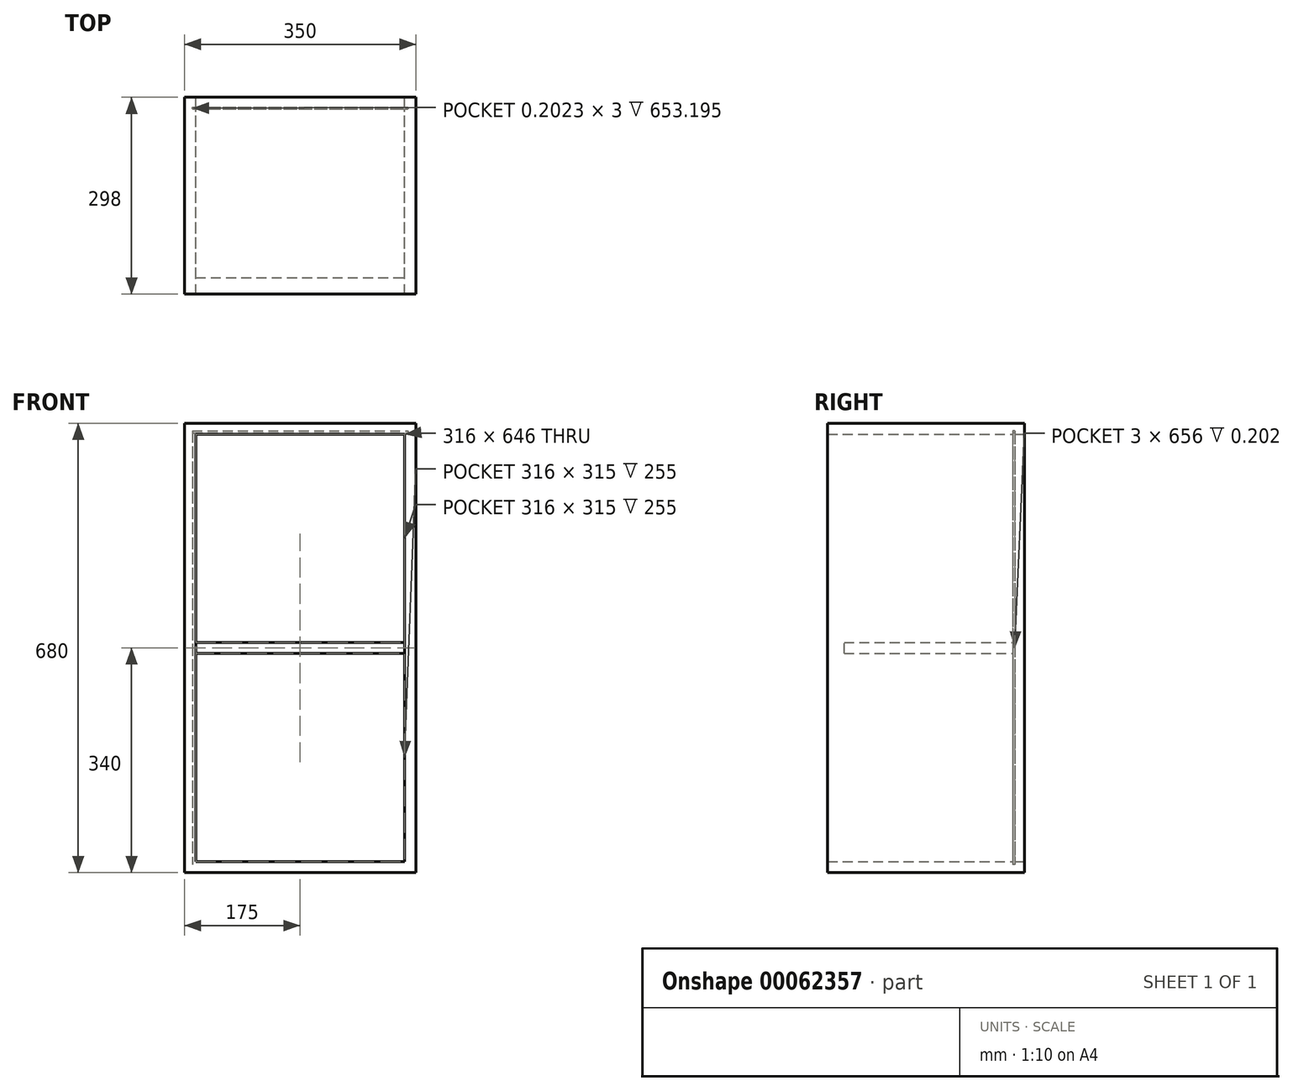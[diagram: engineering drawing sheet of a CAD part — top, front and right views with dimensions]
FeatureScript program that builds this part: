
annotation { "Feature Type Name" : "Feature", "Feature Type Description" : "" }
export const myFeature = defineFeature(function(context is Context, id is Id, definition is map)
    precondition{}
    {
        {
            var Q0;
            Q0=qCreatedBy(makeId("Front.planeOp"),FACE);
            var sketch = newSketch(context, id + "F0", { "sketchPlane" : qUnion([Q0])});
            skLineSegment(sketch, "E0", {"start": v(-175, 340) * mm, "end": v(-175, -340) * mm});
            skLineSegment(sketch, "E1", {"start": v(-175, 340) * mm, "end": v(-158, 323) * mm});
            skLineSegment(sketch, "E2", {"start": v(-158, 323) * mm, "end": v(-158, -323) * mm});
            skLineSegment(sketch, "E3", {"start": v(-158, -323) * mm, "end": v(-175, -340) * mm});
            skLineSegment(sketch, "E4", {"start": v(-175, 340) * mm, "end": v(0, 340) * mm});
            skLineSegment(sketch, "E5", {"start": v(-158, 323) * mm, "end": v(0, 323) * mm});
            skLineSegment(sketch, "E6", {"start": v(-158, -323) * mm, "end": v(0, -323) * mm});
            skLineSegment(sketch, "E7", {"start": v(-175, -340) * mm, "end": v(0, -340) * mm});
            skLineSegment(sketch, "E8", {"start": v(0, 391.01) * mm, "end": v(0, -441.6) * mm, "construction": true});
            skLineSegment(sketch, "E9.MirrorCS", {"start": v(175, 340) * mm, "end": v(0, 340) * mm});
            skLineSegment(sketch, "E10.MirrorCS", {"start": v(158, 323) * mm, "end": v(0, 323) * mm});
            skLineSegment(sketch, "E11.MirrorCS", {"start": v(175, 340) * mm, "end": v(158, 323) * mm});
            skLineSegment(sketch, "E12.MirrorCS", {"start": v(158, 323) * mm, "end": v(158, -323) * mm});
            skLineSegment(sketch, "E13.MirrorCS", {"start": v(175, 340) * mm, "end": v(175, -340) * mm});
            skLineSegment(sketch, "E14.MirrorCS", {"start": v(158, -323) * mm, "end": v(0, -323) * mm});
            skLineSegment(sketch, "E15.MirrorCS", {"start": v(175, -340) * mm, "end": v(0, -340) * mm});
            skLineSegment(sketch, "E16.MirrorCS", {"start": v(158, -323) * mm, "end": v(175, -340) * mm});
            skLineSegment(sketch, "E17", {"start": v(-158, -8) * mm, "end": v(158, -8) * mm});
            skLineSegment(sketch, "E18", {"start": v(158, -8) * mm, "end": v(158, 8) * mm});
            skLineSegment(sketch, "E19", {"start": v(158, 8) * mm, "end": v(-158, 8) * mm});
            skLineSegment(sketch, "E20", {"start": v(-158, 8) * mm, "end": v(-158, -8) * mm});
            skLineSegment(sketch, "E21", {"start": v(-295.4, 0) * mm, "end": v(343.1, 0) * mm, "construction": true});
            skSolve(sketch);
        }
        {
            var Q0;
            Q0=makeQuery(id+"F0.imprint","IMPRINT",FACE,{"disambiguationData":[TD([[makeQuery(id+"F0.imprint","IMPRINT",EDGE,{"derivedFrom":sQuery(id+"F0.wireOp",EDGE,"E1")}),1.0]])]});
            var Q1;
            Q1=makeQuery(id+"F0.imprint","IMPRINT",FACE,{"disambiguationData":[TD([[makeQuery(id+"F0.imprint","IMPRINT",EDGE,{"derivedFrom":sQuery(id+"F0.wireOp",EDGE,"E3")}),1.0]])]});
            var Q2;
            Q2=makeQuery(id+"F0.imprint","IMPRINT",FACE,{"disambiguationData":[TD([[makeQuery(id+"F0.imprint","IMPRINT",EDGE,{"derivedFrom":sQuery(id+"F0.wireOp",EDGE,"E0")}),1.0]])]});
            var Q3;
            {var subQ3=sQuery(id+"F0.wireOp",EDGE,"E11.MirrorCS");Q3=makeQuery(id+"F0.imprint","IMPRINT",FACE,{"disambiguationData":[TD([[makeQuery(id+"F0.imprint","IMPRINT",EDGE,{"derivedFrom":subQ3}),1.0]])]});}
            var Q4;
            Q4=makeQuery(id+"F0.imprint","IMPRINT",FACE,{"disambiguationData":[TD([[makeQuery(id+"F0.imprint","IMPRINT",EDGE,{"derivedFrom":sQuery(id+"F0.wireOp",EDGE,"E17")}),1.0]])]});
            var Q5;
            Q5=sQuery(id+"F0.wireOp",EDGE,"E0");
            var Q6;
            Q6=sQuery(id+"F0.wireOp",EDGE,"E2");
            extrude(context, id + "F1", {"entities" : qUnion([Q0, Q1, Q2, Q3, Q4]), "surfaceEntities" : qUnion([Q5, Q6]), "depth" : 280 * mm, "hasSecondDirection" : true, "secondDirectionOppositeDirection" : true, "secondDirectionDepth" : 18 * mm});
        }
        {
            var Q0;
            Q0=makeQuery(id+"F1.opExtrude","SWEPT_FACE",FACE,{"disambiguationData":[OSD([sQuery(id+"F0.wireOp",EDGE,"E19")])]});
            var sketch = newSketch(context, id + "F2", { "sketchPlane" : qUnion([Q0])});
            skLineSegment(sketch, "E22.bottom", {"start": v(-158, -280) * mm, "end": v(158, -280) * mm});
            skLineSegment(sketch, "E22.top", {"start": v(-158, -255) * mm, "end": v(158, -255) * mm});
            skLineSegment(sketch, "E22.left", {"start": v(-158, -280) * mm, "end": v(-158, -255) * mm});
            skLineSegment(sketch, "E22.right", {"start": v(158, -280) * mm, "end": v(158, -255) * mm});
            skSolve(sketch);
        }
        {
            var Q0;
            Q0=makeQuery(id+"F2.imprint","IMPRINT",FACE,{"disambiguationData":[TD([[makeQuery(id+"F2.imprint","IMPRINT",EDGE,{"derivedFrom":sQuery(id+"F2.wireOp",EDGE,"E22.bottom")}),-1.0]])]});
            extrude(context, id + "F3", {"entities" : qUnion([Q0]), "operationType" : NewBodyOperationType.REMOVE, "oppositeDirection" : true, "depth" : 16 * mm});
        }
        {
            var Q0;
            Q0=makeQuery(id+"F1.opExtrude","SWEPT_FACE",FACE,{"disambiguationData":[OSD([sQuery(id+"F0.wireOp",EDGE,"E17")])]});
            var sketch = newSketch(context, id + "F4", { "sketchPlane" : qUnion([Q0])});
            skLineSegment(sketch, "E23.bottom", {"start": v(-158, -18) * mm, "end": v(158, -18) * mm});
            skLineSegment(sketch, "E23.top", {"start": v(-158, 0) * mm, "end": v(158, 0) * mm});
            skLineSegment(sketch, "E23.left", {"start": v(-158, -18) * mm, "end": v(-158, 0) * mm});
            skLineSegment(sketch, "E23.right", {"start": v(158, -18) * mm, "end": v(158, 0) * mm});
            skSolve(sketch);
        }
        {
            var Q0;
            Q0=makeQuery(id+"F4.imprint","IMPRINT",FACE,{"disambiguationData":[TD([[makeQuery(id+"F4.imprint","IMPRINT",EDGE,{"derivedFrom":sQuery(id+"F4.wireOp",EDGE,"E23.bottom")}),1.0]])]});
            extrude(context, id + "F5", {"entities" : qUnion([Q0]), "operationType" : NewBodyOperationType.REMOVE, "oppositeDirection" : true, "depth" : 16 * mm});
        }
        {
            var Q0;
            Q0=qCreatedBy(makeId("Front.planeOp"),FACE);
            var sketch = newSketch(context, id + "F6", { "sketchPlane" : qUnion([Q0])});
            skLineSegment(sketch, "E24.bottom", {"start": v(-163, 328) * mm, "end": v(163, 328) * mm});
            skLineSegment(sketch, "E24.top", {"start": v(-163, -328) * mm, "end": v(163, -328) * mm});
            skLineSegment(sketch, "E24.left", {"start": v(-163, 328) * mm, "end": v(-163, -328) * mm});
            skLineSegment(sketch, "E24.right", {"start": v(163, 328) * mm, "end": v(163, -328) * mm});
            skLineSegment(sketch, "E25", {"start": v(0, 407.56) * mm, "end": v(0, -373.9) * mm, "construction": true});
            skLineSegment(sketch, "E26", {"start": v(-220.81, 0) * mm, "end": v(218.39, 0) * mm, "construction": true});
            skSolve(sketch);
        }
        {
            var Q0;
            Q0=makeQuery(id+"F6.imprint","IMPRINT",FACE,{"disambiguationData":[TD([[makeQuery(id+"F6.imprint","IMPRINT",EDGE,{"derivedFrom":sQuery(id+"F6.wireOp",EDGE,"E24.bottom")}),-1.0]])]});
            extrude(context, id + "F7", {"entities" : qUnion([Q0]), "operationType" : NewBodyOperationType.REMOVE, "oppositeDirection" : true, "depth" : 3 * mm});
        }
        {
            var Q0;
            Q0=qCreatedBy(makeId("Front.planeOp"),FACE);
            var sketch = newSketch(context, id + "F8", { "sketchPlane" : qUnion([Q0])});
            skLineSegment(sketch, "E27.bottom", {"start": v(-162.8, 325.2) * mm, "end": v(163.2, 325.2) * mm});
            skLineSegment(sketch, "E27.top", {"start": v(-162.8, -330.8) * mm, "end": v(163.2, -330.8) * mm});
            skLineSegment(sketch, "E27.left", {"start": v(-162.8, 325.2) * mm, "end": v(-162.8, -330.8) * mm});
            skLineSegment(sketch, "E27.right", {"start": v(163.2, 325.2) * mm, "end": v(163.2, -330.8) * mm});
            skLineSegment(sketch, "E28", {"start": v(0.2, 404.75) * mm, "end": v(0.2, -376.7) * mm, "construction": true});
            skLineSegment(sketch, "E29", {"start": v(-220.61, -2.8) * mm, "end": v(218.59, -2.8) * mm, "construction": true});
            skSolve(sketch);
        }
        {
            var Q0;
            Q0 = qSketchRegion(id + "F8", true);
            extrude(context, id + "F9", {"entities" : qUnion([Q0]), "operationType" : NewBodyOperationType.ADD, "oppositeDirection" : true, "depth" : 3 * mm});
        }
    });
